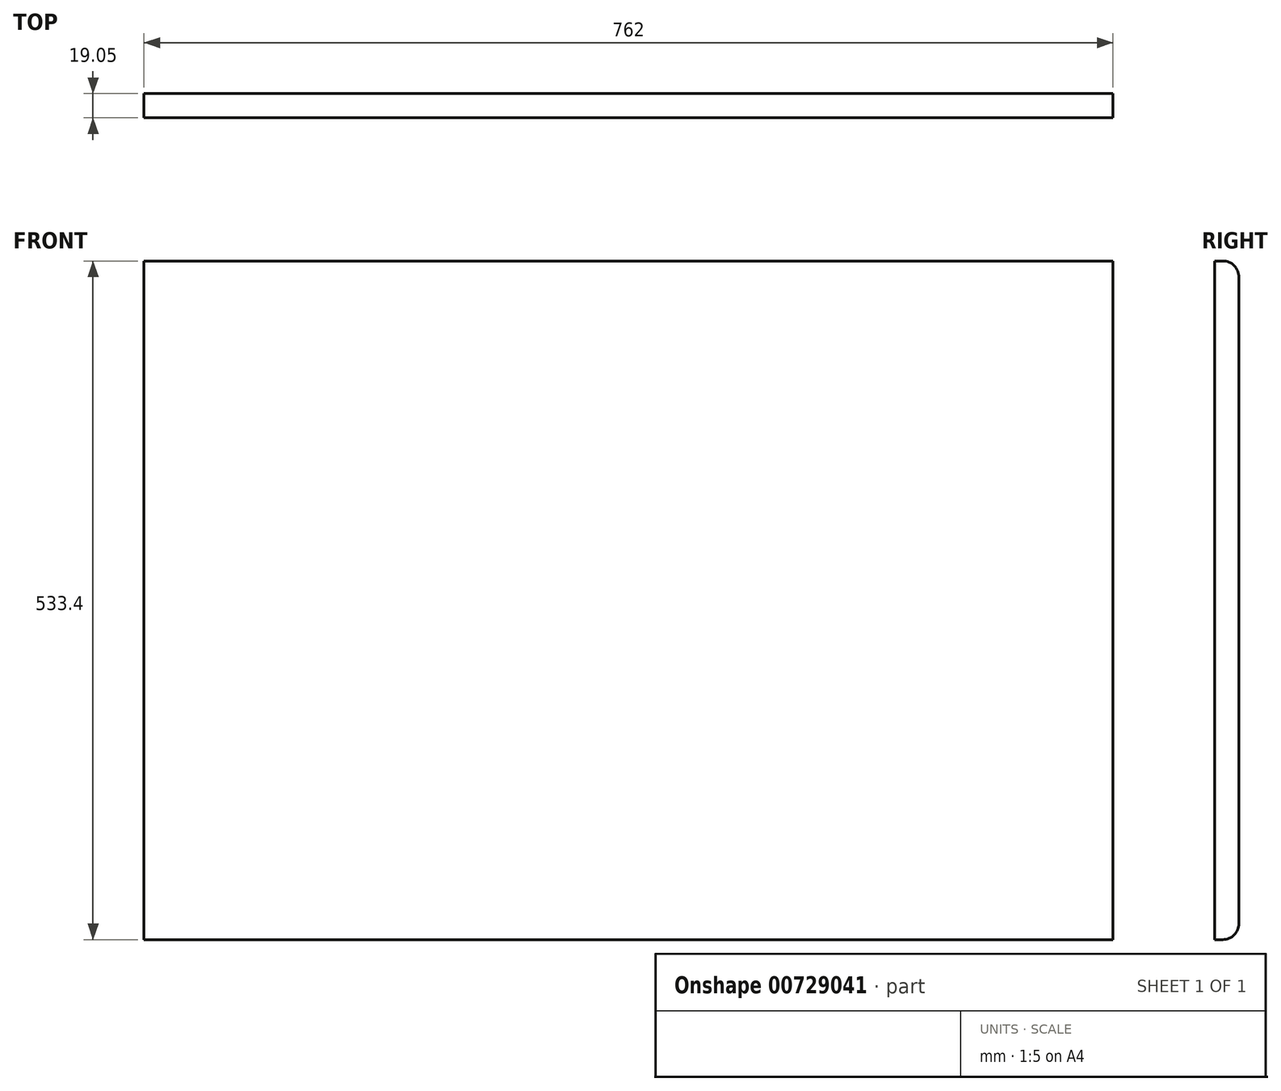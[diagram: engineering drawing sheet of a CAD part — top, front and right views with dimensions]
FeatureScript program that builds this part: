
annotation { "Feature Type Name" : "Feature", "Feature Type Description" : "" }
export const myFeature = defineFeature(function(context is Context, id is Id, definition is map)
    precondition{}
    {
        {
            var Q0;
            Q0=qCreatedBy(makeId("Front.planeOp"),FACE);
            var sketch = newSketch(context, id + "F0", { "sketchPlane" : qUnion([Q0])});
            skLineSegment(sketch, "E0.bottom", {"start": v(-381, -266.7) * mm, "end": v(381, -266.7) * mm});
            skLineSegment(sketch, "E0.top", {"start": v(-381, 266.7) * mm, "end": v(381, 266.7) * mm});
            skLineSegment(sketch, "E0.left", {"start": v(-381, -266.7) * mm, "end": v(-381, 266.7) * mm});
            skLineSegment(sketch, "E0.right", {"start": v(381, -266.7) * mm, "end": v(381, 266.7) * mm});
            skPoint(sketch, "E0.middle", {"position": v(0, 0) * mm});
            skSolve(sketch);
        }
        {
            var Q0;
            Q0 = qSketchRegion(id + "F0", true);
            extrude(context, id + "F1", {"entities" : qUnion([Q0]), "depth" : 19.05 * mm, "offsetDistance" : 25.4 * mm});
        }
        {
            var Q0;
            Q0=makeQuery(id+"F1.opExtrude","CAP_EDGE",EDGE,{"disambiguationData":[OSD([sQuery(id+"F0.wireOp",EDGE,"E0.top")])],"isStart":true});
            var Q1;
            Q1=makeQuery(id+"F1.opExtrude","CAP_EDGE",EDGE,{"disambiguationData":[OSD([sQuery(id+"F0.wireOp",EDGE,"E0.bottom")])],"isStart":true});
            fillet(context, id + "F2", {"entities" : qUnion([Q0, Q1]), "radius" : 12.7 * mm, "tangentPropagation" : true, "allowEdgeOverflow" : false});
        }
    });
